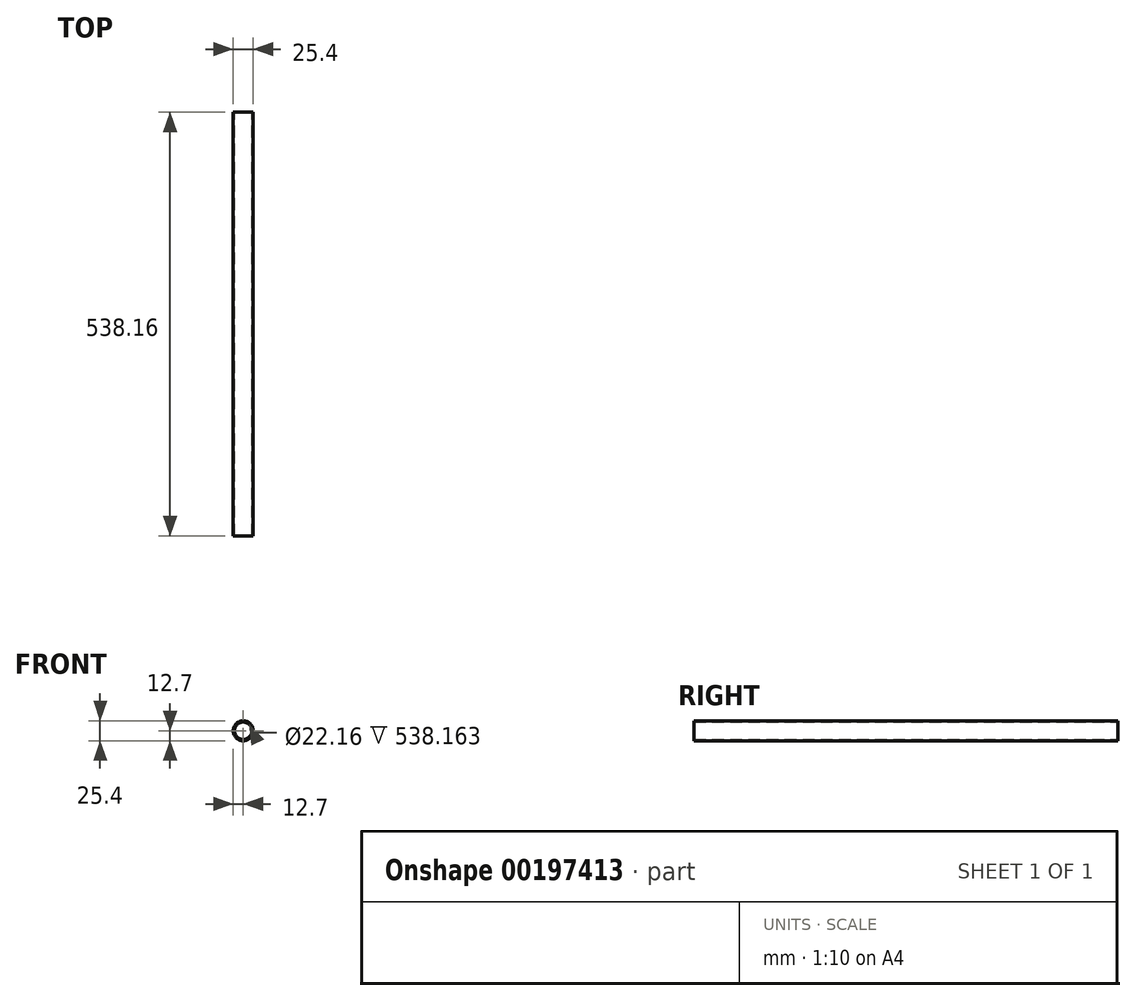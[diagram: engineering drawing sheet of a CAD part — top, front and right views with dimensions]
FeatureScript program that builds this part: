
annotation { "Feature Type Name" : "Feature", "Feature Type Description" : "" }
export const myFeature = defineFeature(function(context is Context, id is Id, definition is map)
    precondition{}
    {
        {
            var Q0;
            Q0=qCreatedBy(makeId("Front.planeOp"),FACE);
            var sketch = newSketch(context, id + "F0", { "sketchPlane" : qUnion([Q0])});
            skCircle(sketch, "E0", {"center": v(0, 0) * mm, "radius": 12.7 * mm});
            skCircle(sketch, "E1.0", {"center": v(0, 0) * mm, "radius": 11.08 * mm});
            skSolve(sketch);
        }
        {
            var Q0;
            Q0 = qSketchRegion(id + "F0", true);
            extrude(context, id + "F1", {"entities" : qUnion([Q0]), "endBound" : BoundingType.SYMMETRIC, "depth" : 538.16 * mm});
        }
    });
